# Revit family: Towel_Bar-DXV-Percy-D357033XX_Series
name_source: partatom
category: Specialty Equipment
revit_build: Autodesk Revit 2014 (Build: 20130308_1515(x64)
units: mm (PartAtom-declared; Revit-internal decimal feet)

## types (3) — shared parameters
Assembly Code = C1030200
Default Elevation = 40"
Finish = Brass-DXV-100-Polished Chrome
Height = 2 1/4"
Installation Type = Surface Mounted
Manufacturer = DXV
Material = Brass-DXV-100-Polished Chrome
Price = Prices may vary. Please consult Manufacturer Representative for most up-to-date price list.
Product Documentation Link = https://dxv01.blob.core.windows.net
Product Page URL = https://www.dxv.com
Revised Date = 12/17/2018
URL = http://www.dxv.com
Warranty Documentation Link = https://www.dxv.com

## per-type parameters (varying)
| type | Base Dia. | Base Radius | Description | Length | Width |
| D35703312.100 | 2 1/8" | 1 1/16" | 12" Grab Bar | 3 7/16" | 11 5/8" |
| D35703318.100 | 2 1/4" | 1 1/8" | 18" Grab Bar | 3 5/8" | 17 1/8" |
| D35703324.100 | 2 1/4" | 1 1/8" | 24" Grab Bar | 3 5/8" | 23 5/8" |

note: column(s) folded — value = type name in every type: Model

## geometry (parser evidence)
native form markers: Sweep x3
no freeform markers — native parametric forms only
